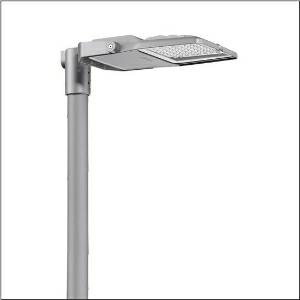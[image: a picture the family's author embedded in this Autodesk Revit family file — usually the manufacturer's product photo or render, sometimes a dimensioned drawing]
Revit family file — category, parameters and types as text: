
# Revit family: floodlight_fl_21_iq_mini___pl43_5xa7771d2a3a_a639
name_source: partatom
category: Lighting Fixtures
units: mm (PartAtom-declared; Revit-internal decimal feet)

## family parameters
Cut with Voids When Loaded = No
Host = Face
Light Source = No
Part Type = Normal
Room Calculation Point = No
Round Connector Dimension = Use Diameter
Shared = No

## types (1)
- --- (1 x LED, 18290 lm, 143 W, 3000K)
    Apparent Load = 143 VA
    CIE Flux Codes = 27 78 99 100 100
    Color Rendering = 70
    Color Temperature = 3000K
    Default Elevation = 1800 mm
    Description = Floodlight FL 21 iQ mini, floodlight, primary light control with lens, of PMMA, primary optical cover: protective disc, of toughened safety glass, transparent, light distribution: PL43, light emission: direct distribution, installation type: surface-mounted, LED, High Power LED, rated luminous flux: 18.290lm, luminous efficacy: 128lm/W, light colour: 730, colour temperature: 3000K, control gear: iQ Comfort/DALI, control: Auto-Match, Temp-Guard, Lumen-Switch, Night-Set, Smart-Wire, Light-Fading, Desk-Remote (wireless, voltage-free reading and setting of iQ features in the workshop via application-optimized NFC function/RFID function), optimised constant luminous flux control (CLO 2.0), with terminal, 6-pole, mains connection: 220..240V, AC, 50/60Hz, start of lifetime: 143W, end of service life: 152W, reduction: 61W, luminaire housing, of diecast aluminium, powder-coated, Siteco® metallic grey (DB 702S), corrosivity category C5 mid according to DIN EN ISO 12944, suitable for swimming pools, chlorine-resistant, sealing non-destructively replaceable, please order mast flange separately, mast bracket, of steel, galvanised, powder-coated, Siteco® metallic grey (DB 702S), protection rating (complete): IP66, insulation class (complete): insulation class II (safety insulation), certification: CE, ENEC, VDE, protection symbol: D, impact resistance: IK08, permissible operating ambient temperature: -40..+40°C, permissible operating ambient temperature for outdoor applications: -40..+50°C, standard: DIN EN 12944, LABS conformity tested according to VDMA 24364:2018-05, packaging unit: 1 piece

Light Distribution: PL43
    Height = 70 mm
    Lamp = 1 x LED
    Lamp Light Flux = 18290 lm
    Lamp Power = 143 W
    Lamp count = 1
    Length = 485 mm
    Luminous efficacy = 128 lm/W
    Manufacturer = Siteco
    ModVariant = No
    Model = 5XA7771D2A3A
    Number of Poles = 1
    OnlyDefault = Yes
    Power Factor = 1
    Product Name = Floodlight FL 21 iQ mini | PL43
    Product group = floodlight | pylon annexe
    ProductGroupID = 6201
    Protection Class = Protection class II
    Protection Degree = IP 66
    RLX_Detail_Level = 1
    RLX_Emergency_Light_Flux = 0 lm
    RLX_Emergency_Type = 0
    RLX_Emergency_Type_DB = No
    RlxData = <blob elided: 101481 chars, md5=6a8e1aa8>
    Socket = socket
    Standby Power = 0 W
    System Light Flux = 18290 lm
    System Power = 143 W
    Type Comments = factory setting: luminous flux: 100 % | dim-lin: 254 | 730 mA
    Type Image = l_1007125.jpg
    URL = http://relux.com
    VarID = @adj_183315
    Voltage = 0 V
    Weight = 0.00 kg
    Width = 337 mm

## geometry (parser evidence)
native form markers: Blend x4, Sweep x12
no freeform markers — native parametric forms only
